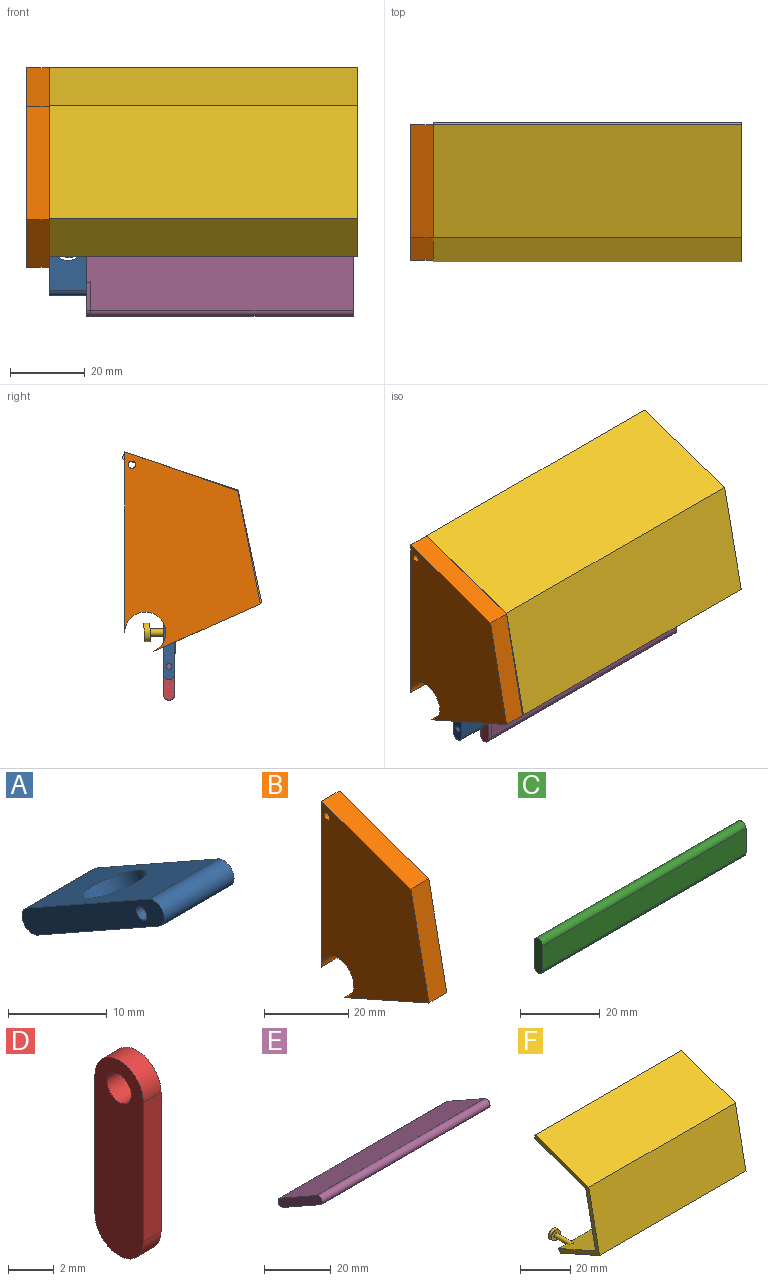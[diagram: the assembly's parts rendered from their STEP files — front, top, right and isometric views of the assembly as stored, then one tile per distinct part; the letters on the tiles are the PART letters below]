
ASSEMBLY  parts=6 mates=7
PART A: 8 faces, bbox 10x20.4x12.8 mm
  f0: plane 17.42x10mm, normal (0,-0.49,-0.87), area 161.5mm2, adj f1,f4,f5,f6,f7
  f1: cylinder r=1.5mm len=10mm, axis (-1,0,0), area 47.1mm2, adj f0,f2,f5,f6
  f2: plane 17.42x10mm, normal (0,0.49,0.87), area 161.5mm2, adj f1,f4,f5,f6,f7
  f3: cylinder r=0.75mm len=10mm, axis (-1,0,0), area 47.1mm2, adj f5,f6
  f4: cylinder r=1.5mm len=10mm, axis (-1,0,0), area 47.1mm2, adj f0,f2,f5,f6
  f5: plane 20.42x12.83mm, normal (1,0,0), area 65.3mm2, adj f0,f1,f2,f3,f4
  f6: plane 20.42x12.83mm, normal (-1,0,0), area 65.3mm2, adj f0,f1,f2,f3,f4
  f7: cylinder r=3.5mm len=7.57mm, axis (0,0.49,0.87), area 66mm2, adj f0,f2
PART B: 8 faces, bbox 6x36.2x53.3 mm
  f0: plane 30.15x6.04mm, normal (0,-0.98,0.2), area 184.5mm2, adj f1,f5,f6,f7
  f1: plane 28.46x12.65mm, normal (0,-0.41,-0.91), area 186.9mm2, adj f0,f2,f6,f7
  f2: cylinder r=5.47mm len=10.95mm, axis (1,0,0), area 141mm2, adj f1,f3,f6,f7
  f3: plane 48.25x6mm, normal (0,1,0), area 289.5mm2, adj f2,f5,f6,f7
  f4: cylinder r=0.98mm len=6mm, axis (1,0,0), area 37.1mm2, adj f6,f7
  f5: plane 30.12x10.46mm, normal (0,-0.33,0.94), area 191.3mm2, adj f0,f3,f6,f7
  f6: plane 53.25x36.16mm, normal (-1,0,0), area 1333.6mm2, adj f0,f1,f2,f3,f4,f5
  f7: plane 53.25x36.16mm, normal (1,0,0), area 1333.6mm2, adj f0,f1,f2,f3,f4,f5
PART C: 6 faces, bbox 72.2x3x10.5 mm
  f0: plane 10.5x3mm, normal (1,0,0), area 29.6mm2, adj f1,f2,f3,f4
  f1: plane 72.2x7.5mm, normal (0,1,0), area 541.5mm2, adj f0,f2,f3,f5
  f2: cylinder r=1.5mm len=72.2mm, axis (-1,0,0), area 340.2mm2, adj f0,f1,f4,f5
  f3: cylinder r=1.5mm len=72.2mm, axis (-1,0,0), area 340.2mm2, adj f0,f1,f4,f5
  f4: plane 72.2x7.5mm, normal (0,-1,0), area 541.5mm2, adj f0,f2,f3,f5
  f5: plane 10.5x3mm, normal (-1,0,0), area 29.6mm2, adj f1,f2,f3,f4
PART D: 7 faces, bbox 1.1x3x10.5 mm
  f0: plane 10.5x3mm, normal (-1,0,0), area 27.8mm2, adj f1,f2,f3,f4,f5
  f1: cylinder r=1.5mm len=3mm, axis (-1,0,0), area 5.2mm2, adj f0,f2,f4,f6
  f2: plane 7.5x1.1mm, normal (0,1,0), area 8.2mm2, adj f0,f1,f3,f6
  f3: cylinder r=1.5mm len=3mm, axis (-1,0,0), area 5.2mm2, adj f0,f2,f4,f6
  f4: plane 7.5x1.1mm, normal (0,-1,0), area 8.2mm2, adj f0,f1,f3,f6
  f5: cylinder r=0.75mm len=1.5mm, axis (-1,0,0), area 5.2mm2, adj f0,f6
  f6: plane 10.5x3mm, normal (1,0,0), area 27.8mm2, adj f1,f2,f3,f4,f5
PART E: 6 faces, bbox 71.1x18.7x11.8 mm
  f0: plane 18.68x11.84mm, normal (1,0,0), area 61.1mm2, adj f1,f3,f4,f5
  f1: cylinder r=1.5mm len=71.1mm, axis (-1,0,0), area 335.1mm2, adj f0,f2,f3,f4
  f2: plane 18.68x11.84mm, normal (-1,0,0), area 61.1mm2, adj f1,f3,f4,f5
  f3: plane 71.1x15.68mm, normal (0,0.49,0.87), area 1279.8mm2, adj f0,f1,f2,f5
  f4: plane 71.1x15.68mm, normal (0,-0.49,-0.87), area 1279.8mm2, adj f0,f1,f2,f5
  f5: cylinder r=1.5mm len=71.1mm, axis (-1,0,0), area 335.1mm2, adj f0,f2,f3,f4
PART F: 14 faces, bbox 82.2x36.8x50.8 mm
  f0: plane 82.2x1.89mm, normal (0,0.94,0.33), area 164.4mm2, adj f1,f3,f6,f9
  f1: plane 50.47x36.81mm, normal (-1,0,0), area 168.4mm2, adj f0,f2,f4,f5,f6,f7,f8,f9
  f2: plane 82.2x1.83mm, normal (0,0.91,-0.41), area 163.5mm2, adj f1,f3,f4,f7,f10
  f3: plane 50.47x36.81mm, normal (1,0,0), area 168.4mm2, adj f0,f2,f4,f5,f6,f7,f8,f9
  f4: plane 82.2x22.2mm, normal (0,-0.41,-0.91), area 1997mm2, adj f1,f2,f3,f5
  f5: plane 82.2x30.15mm, normal (0,-0.98,0.2), area 2527.2mm2, adj f1,f3,f4,f6
  f6: plane 82.2x30.12mm, normal (0,-0.33,0.94), area 2621.1mm2, adj f0,f1,f3,f5
  f7: plane 82.2x20.74mm, normal (0,0.41,0.91), area 1859.6mm2, adj f1,f2,f3,f8,f10
  f8: plane 82.2x27.46mm, normal (0,0.98,-0.2), area 2301.6mm2, adj f1,f3,f7,f9
  f9: plane 82.2x29.04mm, normal (0,0.33,-0.94), area 2527.1mm2, adj f0,f1,f3,f8
  f10: cylinder r=1mm len=9.99mm, axis (0,1,0), area 51.1mm2, adj f2,f7,f12
  f11: cylinder r=2.5mm len=5mm, axis (0,1,0), area 25.1mm2, adj f12,f13
  f12: plane 5x5mm, normal (0,-1,0), area 16.5mm2, adj f10,f11
  f13: plane 5x5mm, normal (0,1,0), area 19.6mm2, adj f11
PLACE A rot(axis=(1,0,0),119.9deg) t=(-24.22,23.96,7.92)mm
PLACE B t=(-24.22,26.81,-28.48)mm fixed
PLACE C t=(-24.22,26.81,-28.48)mm
PLACE D rot(axis=(1,0,0),0deg) t=(-24.22,42.64,-55.32)mm
PLACE E rot(axis=(1,0,0),119.9deg) t=(-25.32,17.46,-3.32)mm
PLACE F rot(axis=(-1,0,0),0.5deg) t=(-24.22,26.3,-28.5)mm
MATE revolute F.f1 <-> B.f4  axis (1,0,0) through (-24.22,24.93,24.74)mm
MATE revolute A.f1 <-> C.f3  axis (1,0,0) through (-14.22,14.86,-11.1)mm
MATE revolute E.f1 <-> C.f2  axis (-1,0,0) through (-14.22,14.86,-18.6)mm
MATE revolute D.f1 <-> E.f5  axis (-1,0,0) through (-14.22,15.02,-36.6)mm
MATE revolute B.f7 <-> A.f1  axis (-1,0,0) through (-24.22,14.86,-11.1)mm
MATE parallel C.f1 <-> B.f3  axis (0,1,0) through (21.88,16.36,-14.85)mm
MATE revolute A.f3 <-> D.f3  axis (1,0,0) through (-14.22,15.02,-29.1)mm
